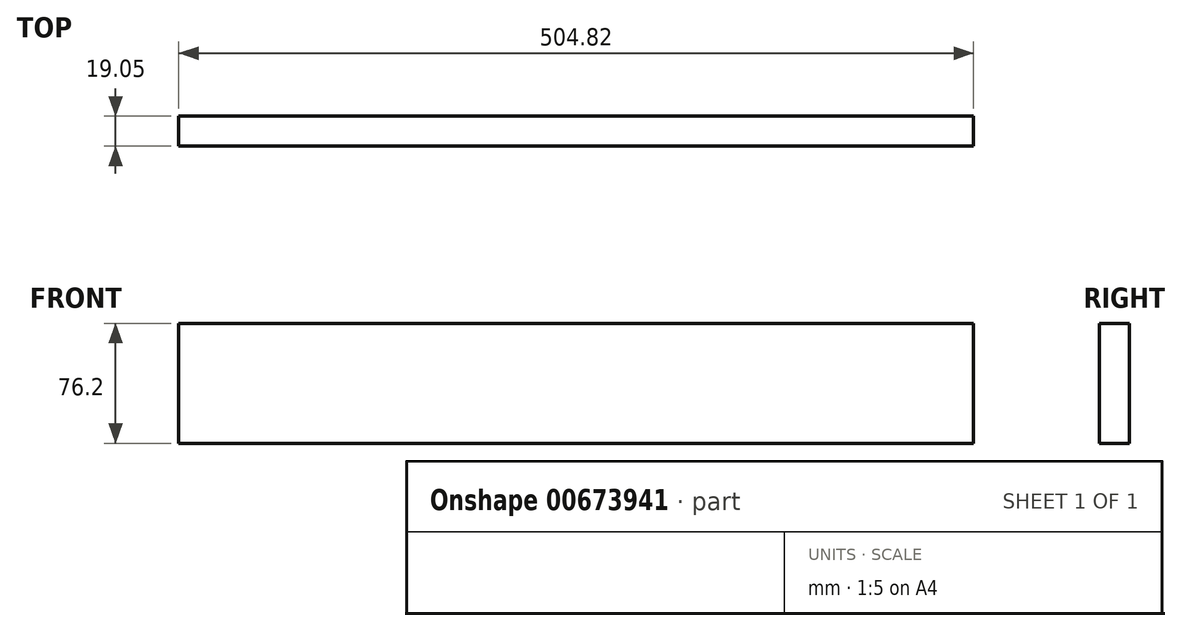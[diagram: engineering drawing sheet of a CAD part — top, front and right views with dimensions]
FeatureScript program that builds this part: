
annotation { "Feature Type Name" : "Feature", "Feature Type Description" : "" }
export const myFeature = defineFeature(function(context is Context, id is Id, definition is map)
    precondition{}
    {
        {
            var Q0;
            Q0=qCreatedBy(makeId("Front.planeOp"),FACE);
            var sketch = newSketch(context, id + "F0", { "sketchPlane" : qUnion([Q0])});
            skLineSegment(sketch, "E0.bottom", {"start": v(-380.64, 89.17) * mm, "end": v(124.18, 89.17) * mm});
            skLineSegment(sketch, "E0.top", {"start": v(-380.64, 12.97) * mm, "end": v(124.18, 12.97) * mm});
            skLineSegment(sketch, "E0.left", {"start": v(-380.64, 89.17) * mm, "end": v(-380.64, 12.97) * mm});
            skLineSegment(sketch, "E0.right", {"start": v(124.18, 89.17) * mm, "end": v(124.18, 12.97) * mm});
            skSolve(sketch);
        }
        {
            var Q0;
            Q0=makeQuery(id+"F0.imprint","IMPRINT",FACE,{"disambiguationData":[TD([[makeQuery(id+"F0.imprint","IMPRINT",EDGE,{"derivedFrom":sQuery(id+"F0.wireOp",EDGE,"E0.bottom")}),-1.0]])]});
            extrude(context, id + "F1", {"entities" : qUnion([Q0]), "depth" : 19.05 * mm, "offsetDistance" : 25.4 * mm});
        }
    });
